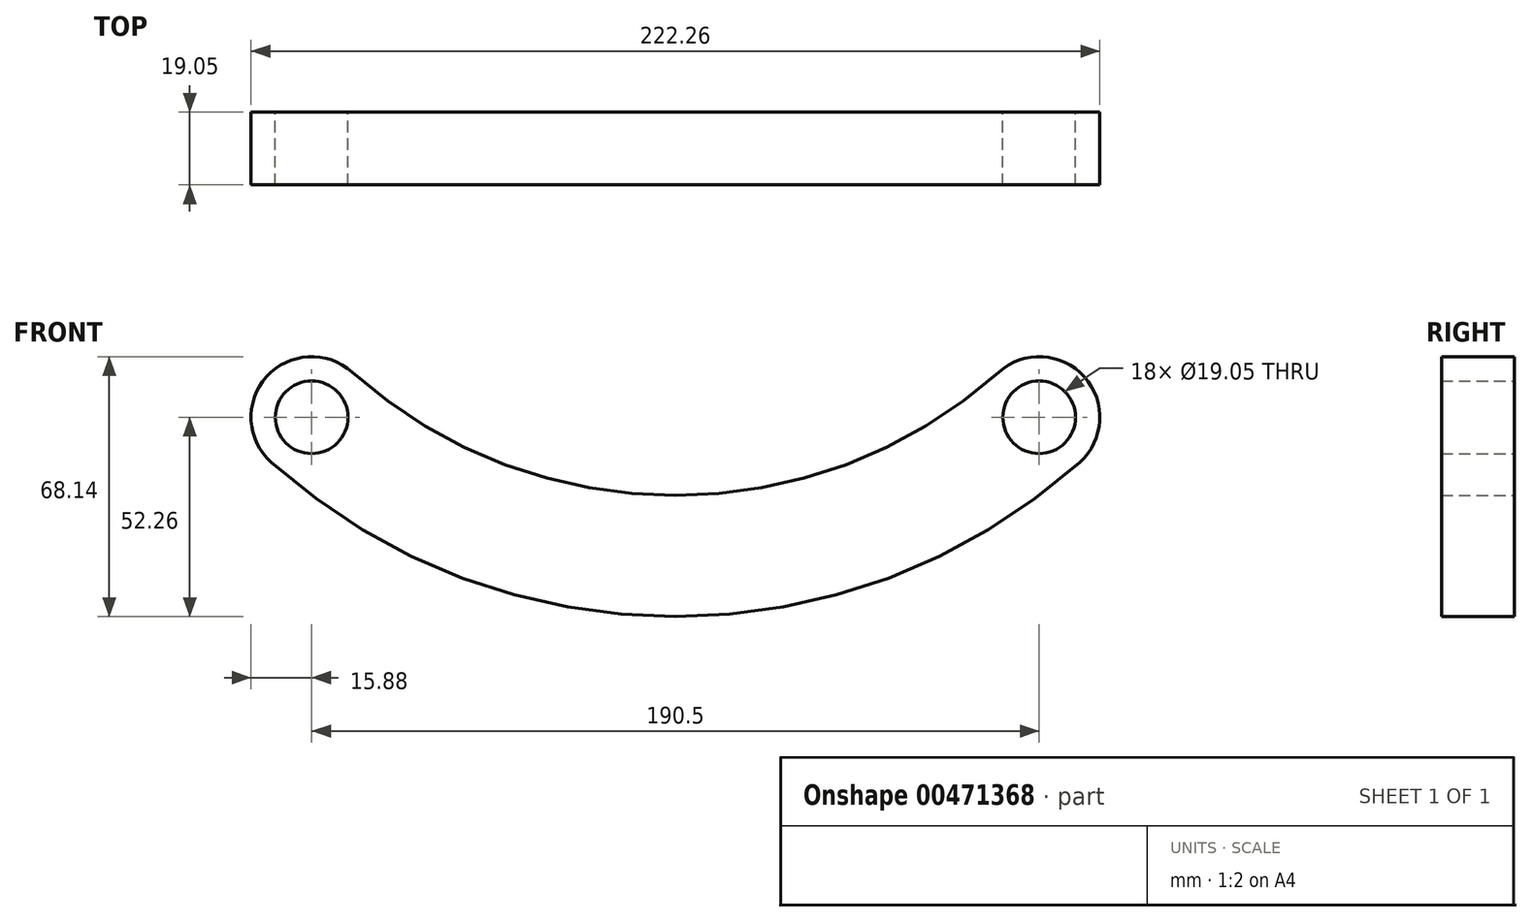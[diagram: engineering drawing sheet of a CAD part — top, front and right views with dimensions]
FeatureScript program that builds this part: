
annotation { "Feature Type Name" : "Feature", "Feature Type Description" : "" }
export const myFeature = defineFeature(function(context is Context, id is Id, definition is map)
    precondition{}
    {
        {
            var Q0;
            Q0=qCreatedBy(makeId("Front.planeOp"),FACE);
            var sketch = newSketch(context, id + "F0", { "sketchPlane" : qUnion([Q0])});
            skCircle(sketch, "E0", {"center": v(0, 0) * mm, "radius": 9.53 * mm});
            skCircle(sketch, "E1", {"center": v(190.5, 0) * mm, "radius": 9.53 * mm});
            skCircle(sketch, "E2", {"center": v(0, 0) * mm, "radius": 15.88 * mm});
            skCircle(sketch, "E3", {"center": v(190.5, 0) * mm, "radius": 15.88 * mm});
            skArc(sketch, "E4", {"start": v(10.58, 11.83) * mm, "mid": v(95.25, -20.5) * mm, "end": v(179.92, 11.83) * mm});
            skArc(sketch, "E5", {"start": v(-10.58, -11.83) * mm, "mid": v(95.25, -52.26) * mm, "end": v(201.08, -11.83) * mm});
            skSolve(sketch);
        }
        {
            var Q0;
            {var subQ0=sQuery(id+"F0.wireOp",EDGE,"E4");Q0=makeQuery(id+"F0.imprint","IMPRINT",FACE,{"disambiguationData":[TD([[makeQuery(id+"F0.imprint","IMPRINT",EDGE,{"derivedFrom":subQ0}),-1.0]])]});}
            var Q1;
            Q1=makeQuery(id+"F0.imprint","IMPRINT",FACE,{"disambiguationData":[TD([[makeQuery(id+"F0.imprint","IMPRINT",EDGE,{"derivedFrom":sQuery(id+"F0.wireOp",EDGE,"E0")}),-1.0]])]});
            var Q2;
            Q2=makeQuery(id+"F0.imprint","IMPRINT",FACE,{"disambiguationData":[TD([[makeQuery(id+"F0.imprint","IMPRINT",EDGE,{"derivedFrom":sQuery(id+"F0.wireOp",EDGE,"E1")}),-1.0]])]});
            extrude(context, id + "F1", {"entities" : qUnion([Q0, Q1, Q2]), "depth" : 19.05 * mm});
        }
    });
